# Revit family: Film_Home_Alone
name_source: partatom
category: Doors
units: mm (PartAtom-declared; Revit-internal decimal feet)

## family parameters
Always vertical = Yes
Cut with Voids When Loaded = No
Host = Wall
OmniClass Number = 23.30.10.00
OmniClass Title = Doors
Room Calculation Point = No
Shared = No

## types (5) — shared parameters
Analytic Construction = Metal
Anschluss Brandmeldeanlage = Yes
Aussentür = Yes
Band Material = <By Category>
Barrierefrei = Yes
Blatt Material = <By Category>
Construction Type Id = MDOOR
Define Thermal Properties by = Schematic Type
Door Material = Door - Panel
Elektroanschluss = Yes
Entrauchungsanlage = Yes
Fassadentür = Yes
Feuchtraum = Yes
Fluchtweg = Yes
Frame Material = Door - Frame
Function = Interior
Heat Transfer Coefficient (U) = 3.7021 W/(m²·K)
Nassraum  = Yes
Oberlicht Füllung Material = <By Category>
Oberlicht Rahmen Material = <By Category>
Rettungsweg = Yes
Steuerung Türzustand = Yes
Thermal Resistance (R) = 0.2701 (m²·K)/W
Thickness = 51 mm  [stored 0.167323 ft]
Trim Projection Ext = 25 mm  [stored 0.082021 ft]
Trim Projection Int = 25 mm  [stored 0.082021 ft]
Trim Width = 76 mm
Tür Oberlicht  = Yes
Tür Seitenteil Links = Yes
Tür Seitenteil Rechts = Yes
Wall Closure = By host
Zarge Material = <By Category>
Zugluftstop = Yes
Öffnungswinkel min = 0.00°
zero-valued in all types: Band Anzahl, Band Tragfähigkeitsklasse, Blatt Breite, Blatt Höhe, Drücker Beanspruchung, Durchgangsbreite min, Durchgangsbreite min SF, Durchgangsbreite nutzbar, Durchgangsbreite nutzbar SF, Durchgangshöhe min, Durchgangshöhe nutzbar, Fluegelanzahl, Plan Detail Architektur, Plan Detail Elektrotechnik, Plan Detail Leitungsplan, Plan Detail Montageplanung, Raum Nr, Raum Nr SR, Solar Heat Gain Coefficient, Tür Bodenhöhe, Tür Bodenhöhe SR, Tür Schwelle Höhe, Visual Light Transmittance, Wand Oberfläche SR Stärke, Wand Oberfläche Stärke, Wand Rohbauöffnung Breite , Wand Rohbauöffnung Höhe , Wand Rohbauöffnung Stärke, Wärmedurchgang, Zarge Außenmaß Breite, Zarge Außenmaß Breite SR, Zarge Maulweite, Zarge Spiegelbreite, Zarge Spiegelbreite SR

## per-type parameters (varying)
| type | Anmerkung | Bauabschnitt | Bauteil  | Freigegeben | Geschoss | Height | ID | Schlisser Höhe | Status | Tür Nummer | Türgriff Höhe | Versions Nr | Width | Zähler Raum |
| 0813 x 2134mm | n.v. | n.v. | Einfamilienhaus, Hintertür | n.v. | EG | 2134 mm | 1 | 2172 mm | Neubau | 1 | 1067 mm | 1 | 813 mm  [stored 2.66732 ft] | 1 |
| 0762 x 2134mm |  |  |  |  |  | 2134 mm |  | 2172 mm |  |  | 1067 mm |  | 762 mm | 0 |
| 0762 x 2032mm |  |  |  |  |  | 2032 mm  [stored 6.66667 ft] |  | 2070 mm  [stored 6.79134 ft] |  |  | 1016 mm  [stored 3.33333 ft] |  | 762 mm | 0 |
| 0915 x 2032mm |  |  |  |  |  | 2032 mm  [stored 6.66667 ft] |  | 2070 mm  [stored 6.79134 ft] |  |  | 1016 mm  [stored 3.33333 ft] |  | 915 mm | 0 |
| 0864 x 2032mm |  |  |  |  |  | 2032 mm  [stored 6.66667 ft] |  | 2070 mm  [stored 6.79134 ft] |  |  | 1016 mm  [stored 3.33333 ft] |  | 864 mm | 0 |

note: [stored X ft] marks values corroborated as IEEE doubles in the binary element streams (Revit-internal decimal feet)

## geometry (parser evidence)
native form markers: Sweep x5
no freeform markers — native parametric forms only
